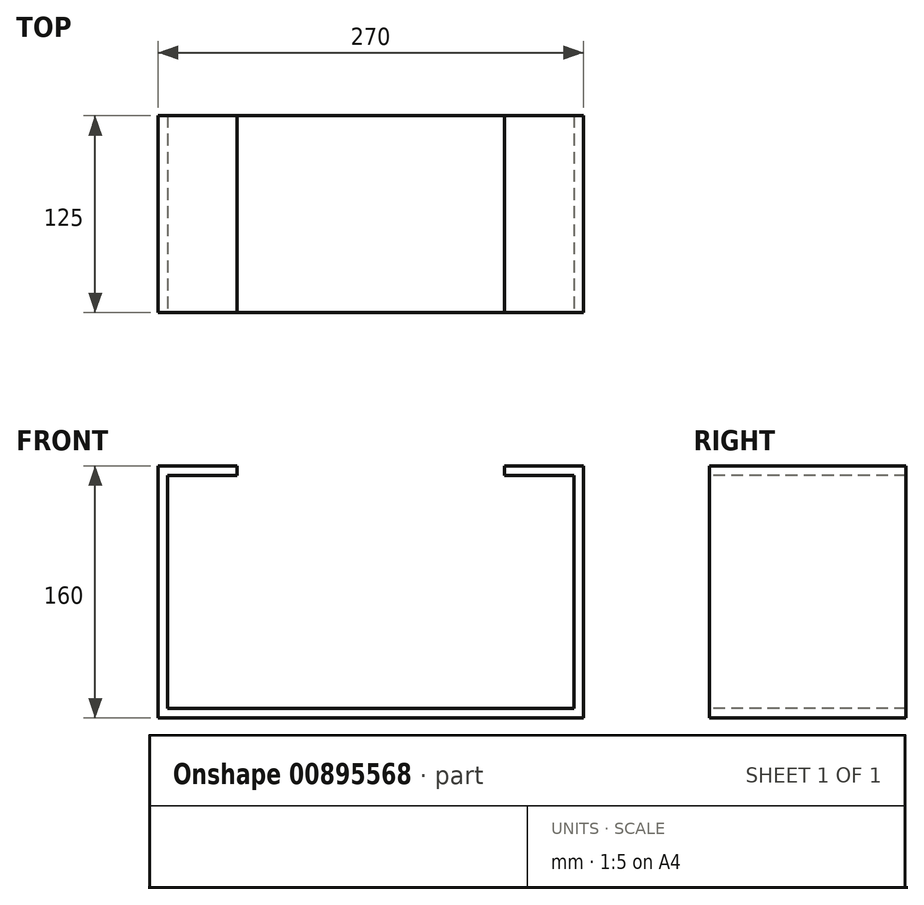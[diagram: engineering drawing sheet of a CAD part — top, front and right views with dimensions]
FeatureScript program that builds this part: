
annotation { "Feature Type Name" : "Feature", "Feature Type Description" : "" }
export const myFeature = defineFeature(function(context is Context, id is Id, definition is map)
    precondition{}
    {
        {
            var Q0;
            Q0=qCreatedBy(makeId("Front.planeOp"),FACE);
            var sketch = newSketch(context, id + "F0", { "sketchPlane" : qUnion([Q0])});
            skLineSegment(sketch, "E0", {"start": v(-98.3, 91.93) * mm, "end": v(-148.3, 91.93) * mm});
            skLineSegment(sketch, "E1", {"start": v(-148.3, 91.93) * mm, "end": v(-148.3, -68.07) * mm});
            skLineSegment(sketch, "E2", {"start": v(-148.3, -68.07) * mm, "end": v(121.7, -68.07) * mm});
            skLineSegment(sketch, "E3", {"start": v(121.7, -68.07) * mm, "end": v(121.7, 91.93) * mm});
            skLineSegment(sketch, "E4", {"start": v(121.7, 91.93) * mm, "end": v(71.7, 91.93) * mm});
            skLineSegment(sketch, "E5", {"start": v(-98.3, 91.93) * mm, "end": v(-98.3, 85.93) * mm});
            skLineSegment(sketch, "E6", {"start": v(-142.3, 85.93) * mm, "end": v(-142.3, -62.07) * mm});
            skLineSegment(sketch, "E7", {"start": v(-142.3, -62.07) * mm, "end": v(115.7, -62.07) * mm});
            skLineSegment(sketch, "E8", {"start": v(115.7, -62.07) * mm, "end": v(115.7, 85.93) * mm});
            skLineSegment(sketch, "E9", {"start": v(115.7, 85.93) * mm, "end": v(71.7, 85.93) * mm});
            skLineSegment(sketch, "E10", {"start": v(71.7, 91.93) * mm, "end": v(71.7, 85.93) * mm});
            skLineSegment(sketch, "E11", {"start": v(-142.3, 85.93) * mm, "end": v(-98.3, 85.93) * mm});
            skSolve(sketch);
        }
        {
            var Q0;
            Q0 = qSketchRegion(id + "F0", true);
            extrude(context, id + "F1", {"entities" : qUnion([Q0]), "oppositeDirection" : true, "depth" : 125 * mm, "offsetDistance" : 25 * mm});
        }
    });
